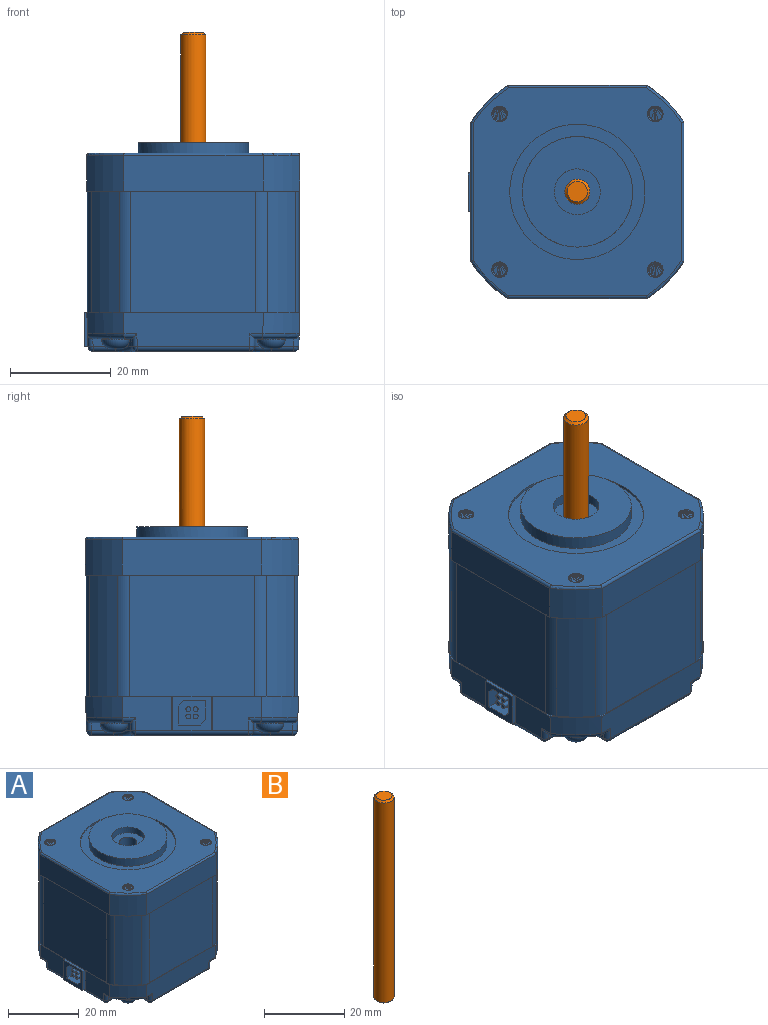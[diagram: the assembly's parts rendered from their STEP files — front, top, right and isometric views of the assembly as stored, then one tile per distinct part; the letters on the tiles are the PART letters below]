
ASSEMBLY  parts=2 mates=1
PART A: 259 faces, bbox 46x46x41.7 mm
  f0: plane 1.69x0.25mm, normal (0,0,-1), area 0.4mm2, adj f61,f87,f105,f247
  f1: plane 2.86x2.83mm, normal (0,0,1), area 5.7mm2, adj f5,f6,f11,f12
  f2: plane 2.86x2.83mm, normal (0,0,1), area 5.7mm2, adj f13,f14,f19,f20
  f3: plane 2.87x2.83mm, normal (0,0,1), area 5.7mm2, adj f21,f22,f27,f28
  f4: plane 2.86x2.83mm, normal (0,0,1), area 5.7mm2, adj f29,f30,f35,f36
  f5: cylinder r=1.5mm len=3.76mm, axis (0,0,1), area 3.8mm2, adj f1,f6,f7,f8,f9,f10,f12,f37
  f6: bspline ~3.05x3.05mm, area 6.4mm2, adj f1,f5,f11
  f7: bspline ~3.05x3.05mm, area 2mm2, adj f5,f11,f37
  f8: bspline ~2.46x2.46mm, area 0mm2, adj f5,f11
  f9: bspline ~3.05x3.05mm, area 4.8mm2, adj f5,f11
  f10: bspline ~2.46x2.46mm, area 0mm2, adj f5,f11
  f11: cylinder r=1.23mm len=3.49mm, axis (0,0,1), area 8mm2, adj f1,f6,f7,f8,f9,f10,f12,f37
  f12: bspline ~4.17x3.53mm, area 17.6mm2, adj f1,f5,f11,f37
  f13: cylinder r=1.5mm len=3.76mm, axis (0,0,1), area 3.8mm2, adj f2,f14,f15,f16,f17,f18,f20,f38
  f14: bspline ~3.05x3.05mm, area 6.4mm2, adj f2,f13,f19
  f15: bspline ~3.05x3.05mm, area 2mm2, adj f13,f19,f38
  f16: bspline ~2.46x2.46mm, area 0mm2, adj f13,f19
  f17: bspline ~3.05x3.05mm, area 4.8mm2, adj f13,f19
  f18: bspline ~2.46x2.46mm, area 0mm2, adj f13,f19
  f19: cylinder r=1.23mm len=3.49mm, axis (0,0,1), area 8mm2, adj f2,f14,f15,f16,f17,f18,f20,f38
  f20: bspline ~4.17x3.53mm, area 17.6mm2, adj f2,f13,f19,f38
  f21: cylinder r=1.5mm len=3.76mm, axis (0,0,1), area 3.8mm2, adj f3,f22,f23,f24,f25,f26,f28,f39
  f22: bspline ~3.05x3.05mm, area 6.4mm2, adj f3,f21,f27
  f23: bspline ~3.05x3.05mm, area 2mm2, adj f21,f27,f39
  f24: bspline ~2.46x2.46mm, area 0mm2, adj f21,f27
  f25: bspline ~3.05x3.05mm, area 4.8mm2, adj f21,f27
  f26: bspline ~2.46x2.46mm, area 0mm2, adj f21,f27
  f27: bspline ~3.74x2.46mm, area 6.7mm2, adj f3,f22,f23,f24,f25,f26,f28,f39
  f28: bspline ~4.17x3.53mm, area 17.6mm2, adj f3,f21,f27,f39
  f29: cylinder r=1.5mm len=3.76mm, axis (0,0,1), area 3.8mm2, adj f4,f30,f31,f32,f33,f34,f36,f41
  f30: bspline ~3.05x3.05mm, area 6.4mm2, adj f4,f29,f35
  f31: bspline ~3.05x3.05mm, area 2mm2, adj f29,f35,f41
  f32: bspline ~2.46x2.46mm, area 0mm2, adj f29,f35
  f33: bspline ~3.05x3.05mm, area 4.8mm2, adj f29,f35
  f34: bspline ~2.46x2.46mm, area 0mm2, adj f29,f35
  f35: cylinder r=1.23mm len=3.49mm, axis (0,0,-1), area 7.3mm2, adj f4,f30,f31,f32,f33,f34,f36,f41
  f36: bspline ~4.17x3.53mm, area 17.6mm2, adj f4,f29,f35,f41
  f37: cone r=1mm half-angle=45deg, axis (0,0,1), area 2.6mm2, adj f5,f7,f11,f12,f42
  f38: cone r=1mm half-angle=45deg, axis (0,0,1), area 2.6mm2, adj f13,f15,f19,f20,f42
  f39: cone r=1mm half-angle=45deg, axis (0,0,1), area 2.6mm2, adj f21,f23,f27,f28,f42
  f40: cylinder r=13.46mm len=26.92mm, axis (0,0,1), area 43mm2, adj f42,f77
  f41: cone r=1mm half-angle=45deg, axis (0,0,1), area 2.6mm2, adj f29,f31,f35,f36,f42
  f42: plane 41.4x41.4mm, normal (0,0,1), area 1030.3mm2, adj f37,f38,f39,f40,f41,f43,f44,f45
  f43: cylinder r=0.51mm len=27.77mm, axis (1,0,0), area 22mm2, adj f42,f44,f50,f51
  f44: torus R=24.84mm, axis (0,0,1), area 8.1mm2, adj f42,f43,f45,f52
  f45: cylinder r=0.51mm len=27.77mm, axis (0,1,0), area 22mm2, adj f42,f44,f46,f53
  f46: torus R=24.84mm, axis (0,0,1), area 8.1mm2, adj f42,f45,f47,f54
  f47: cylinder r=0.51mm len=27.77mm, axis (-1,0,0), area 22mm2, adj f42,f46,f48,f55
  f48: torus R=24.84mm, axis (0,0,1), area 8.1mm2, adj f42,f47,f49,f56
  f49: cylinder r=0.51mm len=27.77mm, axis (0,-1,0), area 22mm2, adj f42,f48,f50,f57
  f50: torus R=24.84mm, axis (0,0,1), area 8.1mm2, adj f42,f43,f49,f58
  f51: plane 27.77x7.06mm, normal (0,-1,0), area 196.1mm2, adj f43,f52,f58,f59
  f52: cylinder r=25.35mm len=7.33mm, axis (0,0,1), area 73.7mm2, adj f44,f51,f53,f59
  f53: plane 27.77x7.06mm, normal (1,0,0), area 196.1mm2, adj f45,f52,f54,f59
  f54: cylinder r=25.35mm len=7.33mm, axis (0,0,1), area 73.7mm2, adj f46,f53,f55,f59
  f55: plane 27.77x7.06mm, normal (0,1,0), area 196.1mm2, adj f47,f54,f56,f59
  f56: cylinder r=25.35mm len=7.33mm, axis (0,0,1), area 73.7mm2, adj f48,f55,f57,f59
  f57: plane 27.77x7.06mm, normal (-1,0,0), area 196.1mm2, adj f49,f56,f58,f59
  f58: cylinder r=25.35mm len=7.33mm, axis (0,0,1), area 73.7mm2, adj f50,f51,f57,f59
  f59: plane 42.42x42.42mm, normal (0,0,-1), area 24.6mm2, adj f51,f52,f53,f54,f55,f56,f57,f58
  f60: plane 1.69x0.25mm, normal (0,0,-1), area 0.4mm2, adj f61,f86,f104,f246
  f61: plane 24.85x24.1mm, normal (-1,0,0), area 598.8mm2, adj f0,f59,f60,f62,f76,f83,f84
  f62: cylinder r=4.01mm len=24.1mm, axis (0,0,1), area 60.9mm2, adj f59,f61,f63,f84
  f63: cylinder r=25.13mm len=24.1mm, axis (0,0,1), area 189.1mm2, adj f59,f62,f64,f84
  f64: cylinder r=4.01mm len=24.1mm, axis (0,0,1), area 60.9mm2, adj f59,f63,f65,f84
  f65: plane 24.85x24.1mm, normal (0,-1,0), area 598.8mm2, adj f59,f64,f66,f84
  f66: cylinder r=4.01mm len=24.1mm, axis (0,0,1), area 60.9mm2, adj f59,f65,f67,f84
  f67: cylinder r=25.13mm len=24.1mm, axis (0,0,1), area 189.1mm2, adj f59,f66,f68,f84
  f68: cylinder r=4.01mm len=24.1mm, axis (0,0,1), area 60.9mm2, adj f59,f67,f69,f84
  f69: plane 24.85x24.1mm, normal (1,0,0), area 598.8mm2, adj f59,f68,f70,f84
  f70: cylinder r=4.01mm len=24.1mm, axis (0,0,1), area 60.9mm2, adj f59,f69,f71,f84
  f71: cylinder r=25.13mm len=24.1mm, axis (0,0,1), area 189.1mm2, adj f59,f70,f72,f84
  f72: cylinder r=4.01mm len=24.1mm, axis (0,0,1), area 60.9mm2, adj f59,f71,f73,f84
  f73: plane 24.85x24.1mm, normal (0,1,0), area 598.8mm2, adj f59,f72,f74,f84
  f74: cylinder r=4.01mm len=24.1mm, axis (0,0,1), area 60.9mm2, adj f59,f73,f75,f84
  f75: cylinder r=25.13mm len=24.1mm, axis (0,0,1), area 189.1mm2, adj f59,f74,f76,f84
  f76: cylinder r=4.01mm len=24.1mm, axis (0,0,1), area 60.9mm2, adj f59,f61,f75,f84
  f77: plane 26.92x26.92mm, normal (0,0,1), area 189.3mm2, adj f40,f78
  f78: cylinder r=11mm len=22mm, axis (0,0,-1), area 175.5mm2, adj f77,f79
  f79: plane 22x22mm, normal (0,0,1), area 314.3mm2, adj f78,f80
  f80: cylinder r=4.57mm len=9.14mm, axis (0,0,1), area 58.4mm2, adj f79,f81
  f81: plane 9.14x9.14mm, normal (0,0,1), area 46.1mm2, adj f80,f82
  f82: cylinder r=2.5mm len=39.49mm, axis (0,0,1), area 619.2mm2, adj f81,f122
  f83: plane 7.62x0.68mm, normal (0,0,1), area 5.1mm2, adj f61,f85,f86,f87
  f84: plane 42.42x42.42mm, normal (0,0,1), area 23.6mm2, adj f61,f62,f63,f64,f65,f66,f67,f68
  f85: plane 7.62x6.8mm, normal (-1,0,0), area 26.3mm2, adj f83,f86,f87,f248,f249,f250,f251,f252
  f86: plane 6.8x2.36mm, normal (0,-1,0), area 15.8mm2, adj f60,f83,f85,f101,f102,f104,f254
  f87: plane 6.8x2.36mm, normal (0,1,0), area 15.8mm2, adj f0,f83,f85,f101,f103,f105,f254
  f88: cylinder r=0.48mm len=1.93mm, axis (1,0,0), area 5.9mm2, adj f100,f258
  f89: cylinder r=0.48mm len=1.93mm, axis (1,0,0), area 5.9mm2, adj f100,f257
  f90: cylinder r=0.48mm len=1.93mm, axis (1,0,0), area 5.9mm2, adj f100,f256
  f91: cylinder r=0.48mm len=1.93mm, axis (1,0,0), area 5.9mm2, adj f100,f255
  f92: torus R=0.84mm, axis (0,0,1), area 37.5mm2, adj f93,f106,f107,f108,f206,f233,f234,f235
  f93: cylinder r=2.75mm len=5.5mm, axis (0,0,1), area 2.2mm2, adj f92,f115,f205
  f94: torus R=0.84mm, axis (0,0,1), area 37.5mm2, adj f95,f109,f110,f111,f204,f220,f221,f222
  f95: cylinder r=2.75mm len=5.5mm, axis (0,0,1), area 2.2mm2, adj f94,f116,f203
  f96: torus R=0.84mm, axis (0,0,1), area 37.5mm2, adj f97,f112,f113,f114,f202,f207,f208,f209
  f97: cylinder r=2.75mm len=5.5mm, axis (0,0,1), area 2.2mm2, adj f96,f117,f201
  f98: torus R=0.84mm, axis (0,0,1), area 37.5mm2, adj f99,f118,f119,f120,f187,f188,f189,f190
  f99: cylinder r=2.75mm len=5.5mm, axis (0,0,1), area 2.2mm2, adj f98,f121,f186
  f100: plane 5.49x4.85mm, normal (-1,0,0), area 22.5mm2, adj f88,f89,f90,f91,f248,f249,f250,f251
  f101: plane 27.77x6.84mm, normal (-1,0,-0.03), area 121.2mm2, adj f84,f86,f87,f102,f103,f124,f127,f142
  f102: plane 1.59x0.25mm, normal (0,0,1), area 0.4mm2, adj f86,f101,f104,f246
  f103: plane 1.59x0.25mm, normal (0,0,1), area 0.4mm2, adj f87,f101,f105,f247
  f104: plane 6.61x0.25mm, normal (-1,0,0), area 1.7mm2, adj f60,f86,f102,f246
  f105: plane 6.61x0.25mm, normal (-1,0,0), area 1.7mm2, adj f0,f87,f103,f247
  f106: plane 0.62x0.62mm, normal (0,0,-1), area 0.3mm2, adj f92,f238,f239
  f107: plane 0.62x0.62mm, normal (0,0,-1), area 0.3mm2, adj f92,f240,f241
  f108: plane 0.62x0.62mm, normal (0,0,-1), area 0.3mm2, adj f92,f242,f243
  f109: plane 0.62x0.62mm, normal (0,0,-1), area 0.3mm2, adj f94,f225,f226
  f110: plane 0.62x0.62mm, normal (0,0,-1), area 0.3mm2, adj f94,f227,f228
  f111: plane 0.62x0.62mm, normal (0,0,-1), area 0.3mm2, adj f94,f229,f230
  f112: plane 0.62x0.62mm, normal (0,0,-1), area 0.3mm2, adj f96,f212,f213
  f113: plane 0.62x0.62mm, normal (0,0,-1), area 0.3mm2, adj f96,f214,f215
  f114: plane 0.62x0.62mm, normal (0,0,-1), area 0.3mm2, adj f96,f216,f217
  f115: plane 7.81x7.81mm, normal (0,0,-1), area 17.4mm2, adj f93,f136,f137,f138,f142,f143,f145,f148
  f116: plane 7.81x7.81mm, normal (0,0,-1), area 17.4mm2, adj f95,f139,f140,f141,f159,f163,f167,f170
  f117: plane 7.81x7.81mm, normal (0,0,-1), area 17.4mm2, adj f97,f130,f131,f132,f149,f153,f156,f160
  f118: plane 0.62x0.62mm, normal (0,0,-1), area 0.3mm2, adj f98,f193,f194
  f119: plane 0.62x0.62mm, normal (0,0,-1), area 0.3mm2, adj f98,f195,f196
  f120: plane 0.62x0.62mm, normal (0,0,-1), area 0.3mm2, adj f98,f197,f198
  f121: plane 7.81x7.81mm, normal (0,0,-1), area 17.4mm2, adj f99,f133,f134,f135,f171,f172,f176,f179
  f122: plane 39.91x39.91mm, normal (0,0,-1), area 1280.7mm2, adj f82,f144,f147,f150,f151,f157,f158,f161
  f123: cone r=0.03mm half-angle=2deg, axis (0,0,1), area 44.6mm2, adj f84,f126,f129,f167
  f124: cone r=0.03mm half-angle=2deg, axis (0,0,1), area 44.6mm2, adj f84,f101,f126,f145
  f125: cone r=0.03mm half-angle=2deg, axis (0,0,1), area 44.6mm2, adj f84,f128,f129,f176
  f126: plane 27.77x6.84mm, normal (0,-1,-0.03), area 176.3mm2, adj f84,f123,f124,f148,f152,f158,f159,f163
  f127: cone r=0.03mm half-angle=2deg, axis (0,0,1), area 44.6mm2, adj f84,f101,f128,f156
  f128: plane 27.77x6.84mm, normal (0,1,-0.03), area 176.3mm2, adj f84,f125,f127,f160,f164,f171,f172,f173
  f129: plane 27.77x6.84mm, normal (1,0,-0.03), area 176.3mm2, adj f84,f123,f125,f170,f175,f179,f181,f182
  f130: plane 4.47x1.56mm, normal (-1,0,-0.03), area 6.9mm2, adj f117,f131,f164,f165
  f131: cone r=0.03mm half-angle=2deg, axis (0,0,-1), area 8.2mm2, adj f117,f130,f132,f161
  f132: plane 4.47x1.56mm, normal (0,1,-0.03), area 6.9mm2, adj f117,f131,f149,f157
  f133: plane 4.47x1.56mm, normal (0,1,-0.03), area 6.9mm2, adj f121,f134,f182,f185
  f134: cone r=0.03mm half-angle=2deg, axis (0,0,-1), area 8.2mm2, adj f121,f133,f135,f183
  f135: plane 4.47x1.56mm, normal (1,0,-0.03), area 6.9mm2, adj f121,f134,f172,f180
  f136: plane 4.47x1.56mm, normal (0,-1,-0.03), area 6.9mm2, adj f115,f137,f143,f144
  f137: cone r=0.03mm half-angle=2deg, axis (0,0,-1), area 8.2mm2, adj f115,f136,f138,f147
  f138: plane 4.47x1.56mm, normal (-1,0,-0.03), area 6.9mm2, adj f115,f137,f151,f152
  f139: cone r=0.03mm half-angle=2deg, axis (0,0,-1), area 8.2mm2, adj f116,f140,f141,f169
  f140: plane 4.47x1.56mm, normal (0,-1,-0.03), area 6.9mm2, adj f116,f139,f174,f175
  f141: plane 4.47x1.56mm, normal (1,0,-0.03), area 6.9mm2, adj f116,f139,f159,f166
  f142: cylinder r=1.02mm len=2.58mm, axis (0,-1,0), area 3mm2, adj f101,f115,f143,f145
  f143: cylinder r=1.02mm len=2.55mm, axis (-0.03,-0.03,1), area 3.1mm2, adj f101,f115,f136,f142,f146
  f144: cylinder r=1.02mm len=4.42mm, axis (-1,0,0), area 6.9mm2, adj f122,f136,f146,f147
  f145: torus R=24.18mm, axis (0,0,-1), area 15.3mm2, adj f115,f124,f142,f148,f205
  f146: sphere r=1.02mm, area 1mm2, adj f143,f144,f150
  f147: torus R=4.37mm, axis (0,0,1), area 9.2mm2, adj f122,f137,f144,f151
  f148: cylinder r=1.02mm len=2.58mm, axis (1,0,0), area 3mm2, adj f115,f126,f145,f152
  f149: cylinder r=1.02mm len=2.55mm, axis (0.03,-0.03,-1), area 3.1mm2, adj f101,f117,f132,f153,f154
  f150: cylinder r=1.02mm len=22.33mm, axis (0,1,0), area 34.9mm2, adj f101,f122,f146,f154
  f151: cylinder r=1.02mm len=4.42mm, axis (0,1,0), area 6.9mm2, adj f122,f138,f147,f155
  f152: cylinder r=1.02mm len=2.55mm, axis (0.03,0.03,-1), area 3.1mm2, adj f115,f126,f138,f148,f155
  f153: cylinder r=1.02mm len=2.58mm, axis (0,-1,0), area 3mm2, adj f101,f117,f149,f156
  f154: sphere r=1.02mm, area 1mm2, adj f149,f150,f157
  f155: sphere r=1.02mm, area 1mm2, adj f151,f152,f158
  f156: torus R=24.18mm, axis (0,0,1), area 15.3mm2, adj f117,f127,f153,f160,f201
  f157: cylinder r=1.02mm len=4.42mm, axis (1,0,0), area 6.9mm2, adj f122,f132,f154,f161
  f158: cylinder r=1.02mm len=22.33mm, axis (-1,0,0), area 34.9mm2, adj f122,f126,f155,f162
  f159: cylinder r=1.02mm len=2.55mm, axis (0.03,-0.03,1), area 3.1mm2, adj f116,f126,f141,f162,f163
  f160: cylinder r=1.02mm len=2.58mm, axis (-1,0,0), area 3mm2, adj f117,f128,f156,f164
  f161: torus R=4.37mm, axis (0,0,1), area 9.2mm2, adj f122,f131,f157,f165
  f162: sphere r=1.02mm, area 1mm2, adj f158,f159,f166
  f163: cylinder r=1.02mm len=2.58mm, axis (1,0,0), area 3mm2, adj f116,f126,f159,f167
  f164: cylinder r=1.02mm len=2.55mm, axis (-0.03,0.03,1), area 3.1mm2, adj f117,f128,f130,f160,f168
  f165: cylinder r=1.02mm len=4.42mm, axis (0,1,0), area 6.9mm2, adj f122,f130,f161,f168
  f166: cylinder r=1.02mm len=4.42mm, axis (0,-1,0), area 6.9mm2, adj f122,f141,f162,f169
  f167: torus R=24.18mm, axis (0,0,-1), area 15.3mm2, adj f116,f123,f163,f170,f203
  f168: sphere r=1.02mm, area 1mm2, adj f164,f165,f173
  f169: torus R=4.37mm, axis (0,0,1), area 9.2mm2, adj f122,f139,f166,f174
  f170: cylinder r=1.02mm len=2.58mm, axis (0,1,0), area 3mm2, adj f116,f129,f167,f175
  f171: cylinder r=1.02mm len=2.58mm, axis (-1,0,0), area 3mm2, adj f121,f128,f172,f176
  f172: cylinder r=1.02mm len=2.55mm, axis (-0.03,-0.03,-1), area 3.1mm2, adj f121,f128,f135,f171,f177
  f173: cylinder r=1.02mm len=22.33mm, axis (1,0,0), area 34.9mm2, adj f122,f128,f168,f177
  f174: cylinder r=1.02mm len=4.42mm, axis (-1,0,0), area 6.9mm2, adj f122,f140,f169,f178
  f175: cylinder r=1.02mm len=2.55mm, axis (-0.03,0.03,-1), area 3.1mm2, adj f116,f129,f140,f170,f178
  f176: torus R=24.18mm, axis (0,0,-1), area 15.3mm2, adj f121,f125,f171,f179,f186
  f177: sphere r=1.02mm, area 1mm2, adj f172,f173,f180
  f178: sphere r=1.02mm, area 1mm2, adj f174,f175,f181
  f179: cylinder r=1.02mm len=2.58mm, axis (0,1,0), area 3mm2, adj f121,f129,f176,f182
  f180: cylinder r=1.02mm len=4.42mm, axis (0,-1,0), area 6.9mm2, adj f122,f135,f177,f183
  f181: cylinder r=1.02mm len=22.33mm, axis (0,-1,0), area 34.9mm2, adj f122,f129,f178,f184
  f182: cylinder r=1.02mm len=2.55mm, axis (0.03,0.03,1), area 3.1mm2, adj f121,f129,f133,f179,f184
  f183: torus R=4.37mm, axis (0,0,1), area 9.2mm2, adj f122,f134,f180,f185
  f184: sphere r=1.02mm, area 1mm2, adj f181,f182,f185
  f185: cylinder r=1.02mm len=4.42mm, axis (1,0,0), area 6.9mm2, adj f122,f133,f183,f184
  f186: plane 2.3x2.3mm, normal (0,0,1), area 1.1mm2, adj f99,f176
  f187: plane 0.62x0.62mm, normal (0,0,-1), area 0.3mm2, adj f98,f192,f199
  f188: plane 1.44x0.44mm, normal (1,0,0), area 0.6mm2, adj f98,f192,f193,f200
  f189: plane 1.42x0.41mm, normal (0,1,0), area 0.6mm2, adj f98,f194,f195,f200
  f190: plane 1.44x0.44mm, normal (-1,0,0), area 0.6mm2, adj f98,f196,f197,f200
  f191: plane 1.42x0.41mm, normal (0,-1,0), area 0.6mm2, adj f98,f198,f199,f200
  f192: plane 1.56x1.33mm, normal (0,-1,0), area 1.9mm2, adj f98,f187,f188,f199,f200
  f193: plane 1.56x1.33mm, normal (0,1,0), area 1.9mm2, adj f98,f118,f188,f194,f200
  f194: plane 1.56x1.33mm, normal (1,0,0), area 1.9mm2, adj f98,f118,f189,f193,f200
  f195: plane 1.56x1.33mm, normal (-1,0,0), area 1.9mm2, adj f98,f119,f189,f196,f200
  f196: plane 1.56x1.33mm, normal (0,1,0), area 1.9mm2, adj f98,f119,f190,f195,f200
  f197: plane 1.56x1.33mm, normal (0,-1,0), area 1.9mm2, adj f98,f120,f190,f198,f200
  f198: plane 1.56x1.33mm, normal (-1,0,0), area 1.9mm2, adj f98,f120,f191,f197,f200
  f199: plane 1.56x1.33mm, normal (1,0,0), area 1.9mm2, adj f98,f187,f191,f192,f200
  f200: plane 3x3mm, normal (0,0,-1), area 2.3mm2, adj f188,f189,f190,f191,f192,f193,f194,f195
  f201: plane 2.3x2.3mm, normal (0,0,1), area 1.1mm2, adj f97,f156
  f202: plane 0.62x0.62mm, normal (0,0,-1), area 0.3mm2, adj f96,f211,f218
  f203: plane 2.3x2.3mm, normal (0,0,1), area 1.1mm2, adj f95,f167
  f204: plane 0.62x0.62mm, normal (0,0,-1), area 0.3mm2, adj f94,f224,f231
  f205: plane 2.3x2.3mm, normal (0,0,1), area 1.1mm2, adj f93,f145
  f206: plane 0.62x0.62mm, normal (0,0,-1), area 0.3mm2, adj f92,f237,f244
  f207: plane 1.44x0.44mm, normal (1,0,0), area 0.6mm2, adj f96,f211,f212,f219
  f208: plane 1.42x0.41mm, normal (0,1,0), area 0.6mm2, adj f96,f213,f214,f219
  f209: plane 1.44x0.44mm, normal (-1,0,0), area 0.6mm2, adj f96,f215,f216,f219
  f210: plane 1.42x0.41mm, normal (0,-1,0), area 0.6mm2, adj f96,f217,f218,f219
  f211: plane 1.56x1.33mm, normal (0,-1,0), area 1.9mm2, adj f96,f202,f207,f218,f219
  f212: plane 1.56x1.33mm, normal (0,1,0), area 1.9mm2, adj f96,f112,f207,f213,f219
  f213: plane 1.56x1.33mm, normal (1,0,0), area 1.9mm2, adj f96,f112,f208,f212,f219
  f214: plane 1.56x1.33mm, normal (-1,0,0), area 1.9mm2, adj f96,f113,f208,f215,f219
  f215: plane 1.56x1.33mm, normal (0,1,0), area 1.9mm2, adj f96,f113,f209,f214,f219
  f216: plane 1.56x1.33mm, normal (0,-1,0), area 1.9mm2, adj f96,f114,f209,f217,f219
  f217: plane 1.56x1.33mm, normal (-1,0,0), area 1.9mm2, adj f96,f114,f210,f216,f219
  f218: plane 1.56x1.33mm, normal (1,0,0), area 1.9mm2, adj f96,f202,f210,f211,f219
  f219: plane 3x3mm, normal (0,0,-1), area 2.3mm2, adj f207,f208,f209,f210,f211,f212,f213,f214
  f220: plane 1.44x0.44mm, normal (1,0,0), area 0.6mm2, adj f94,f224,f225,f232
  f221: plane 1.42x0.41mm, normal (0,1,0), area 0.6mm2, adj f94,f226,f227,f232
  f222: plane 1.44x0.44mm, normal (-1,0,0), area 0.6mm2, adj f94,f228,f229,f232
  f223: plane 1.42x0.41mm, normal (0,-1,0), area 0.6mm2, adj f94,f230,f231,f232
  f224: plane 1.56x1.33mm, normal (0,-1,0), area 1.9mm2, adj f94,f204,f220,f231,f232
  f225: plane 1.56x1.33mm, normal (0,1,0), area 1.9mm2, adj f94,f109,f220,f226,f232
  f226: plane 1.56x1.33mm, normal (1,0,0), area 1.9mm2, adj f94,f109,f221,f225,f232
  f227: plane 1.56x1.33mm, normal (-1,0,0), area 1.9mm2, adj f94,f110,f221,f228,f232
  f228: plane 1.56x1.33mm, normal (0,1,0), area 1.9mm2, adj f94,f110,f222,f227,f232
  f229: plane 1.56x1.33mm, normal (0,-1,0), area 1.9mm2, adj f94,f111,f222,f230,f232
  f230: plane 1.56x1.33mm, normal (-1,0,0), area 1.9mm2, adj f94,f111,f223,f229,f232
  f231: plane 1.56x1.33mm, normal (1,0,0), area 1.9mm2, adj f94,f204,f223,f224,f232
  f232: plane 3x3mm, normal (0,0,-1), area 2.3mm2, adj f220,f221,f222,f223,f224,f225,f226,f227
  f233: plane 1.44x0.44mm, normal (1,0,0), area 0.6mm2, adj f92,f237,f238,f245
  f234: plane 1.42x0.41mm, normal (0,1,0), area 0.6mm2, adj f92,f239,f240,f245
  f235: plane 1.44x0.44mm, normal (-1,0,0), area 0.6mm2, adj f92,f241,f242,f245
  f236: plane 1.42x0.41mm, normal (0,-1,0), area 0.6mm2, adj f92,f243,f244,f245
  f237: plane 1.56x1.33mm, normal (0,-1,0), area 1.9mm2, adj f92,f206,f233,f244,f245
  f238: plane 1.56x1.33mm, normal (0,1,0), area 1.9mm2, adj f92,f106,f233,f239,f245
  f239: plane 1.56x1.33mm, normal (1,0,0), area 1.9mm2, adj f92,f106,f234,f238,f245
  f240: plane 1.56x1.33mm, normal (-1,0,0), area 1.9mm2, adj f92,f107,f234,f241,f245
  f241: plane 1.56x1.33mm, normal (0,1,0), area 1.9mm2, adj f92,f107,f235,f240,f245
  f242: plane 1.56x1.33mm, normal (0,-1,0), area 1.9mm2, adj f92,f108,f235,f243,f245
  f243: plane 1.56x1.33mm, normal (-1,0,0), area 1.9mm2, adj f92,f108,f236,f242,f245
  f244: plane 1.56x1.33mm, normal (1,0,0), area 1.9mm2, adj f92,f206,f236,f237,f245
  f245: plane 3x3mm, normal (0,0,-1), area 2.3mm2, adj f233,f234,f235,f236,f237,f238,f239,f240
  f246: plane 6.61x1.82mm, normal (0,1,0), area 11.2mm2, adj f60,f84,f101,f102,f104
  f247: plane 6.61x1.82mm, normal (0,-1,0), area 11.2mm2, adj f0,f84,f101,f103,f105
  f248: plane 4.41x2.36mm, normal (0,0,-1), area 10.4mm2, adj f85,f100,f249,f253
  f249: plane 2.36x1.08mm, normal (0,-0.71,-0.71), area 3.6mm2, adj f85,f100,f248,f250
  f250: plane 3.77x2.36mm, normal (0,-1,0), area 8.9mm2, adj f85,f100,f249,f251
  f251: plane 4.41x2.36mm, normal (0,0,1), area 10.4mm2, adj f85,f100,f250,f252
  f252: plane 2.36x1.08mm, normal (0,0.71,0.71), area 3.6mm2, adj f85,f100,f251,f253
  f253: plane 3.77x2.36mm, normal (0,1,0), area 8.9mm2, adj f85,f100,f248,f252
  f254: plane 7.62x0.79mm, normal (0,0,-1), area 6mm2, adj f85,f86,f87,f101
  f255: plane 0.97x0.97mm, normal (-1,0,0), area 0.7mm2, adj f91
  f256: plane 0.97x0.97mm, normal (-1,0,0), area 0.7mm2, adj f90
  f257: plane 0.97x0.97mm, normal (-1,0,0), area 0.7mm2, adj f89
  f258: plane 0.97x0.97mm, normal (-1,0,0), area 0.7mm2, adj f88
PART B: 5 faces, bbox 5x5x62 mm
  f0: cylinder r=2.5mm len=61mm, axis (0,0,-1), area 958.2mm2, adj f3,f4
  f1: plane 4x4mm, normal (0,0,1), area 12.6mm2, adj f3
  f2: plane 4x4mm, normal (0,0,-1), area 12.6mm2, adj f4
  f3: cone r=2.5mm half-angle=45deg, axis (0,0,-1), area 10mm2, adj f0,f1
  f4: cone r=2mm half-angle=45deg, axis (0,0,1), area 10mm2, adj f0,f2
PLACE A t=(237.38,-137.62,349.47)mm
PLACE B t=(274.95,-138.24,350.97)mm
MATE revolute B.f0 <-> A.f78  axis (0,0,-1) through (12.12,4.77,-21.87)mm
